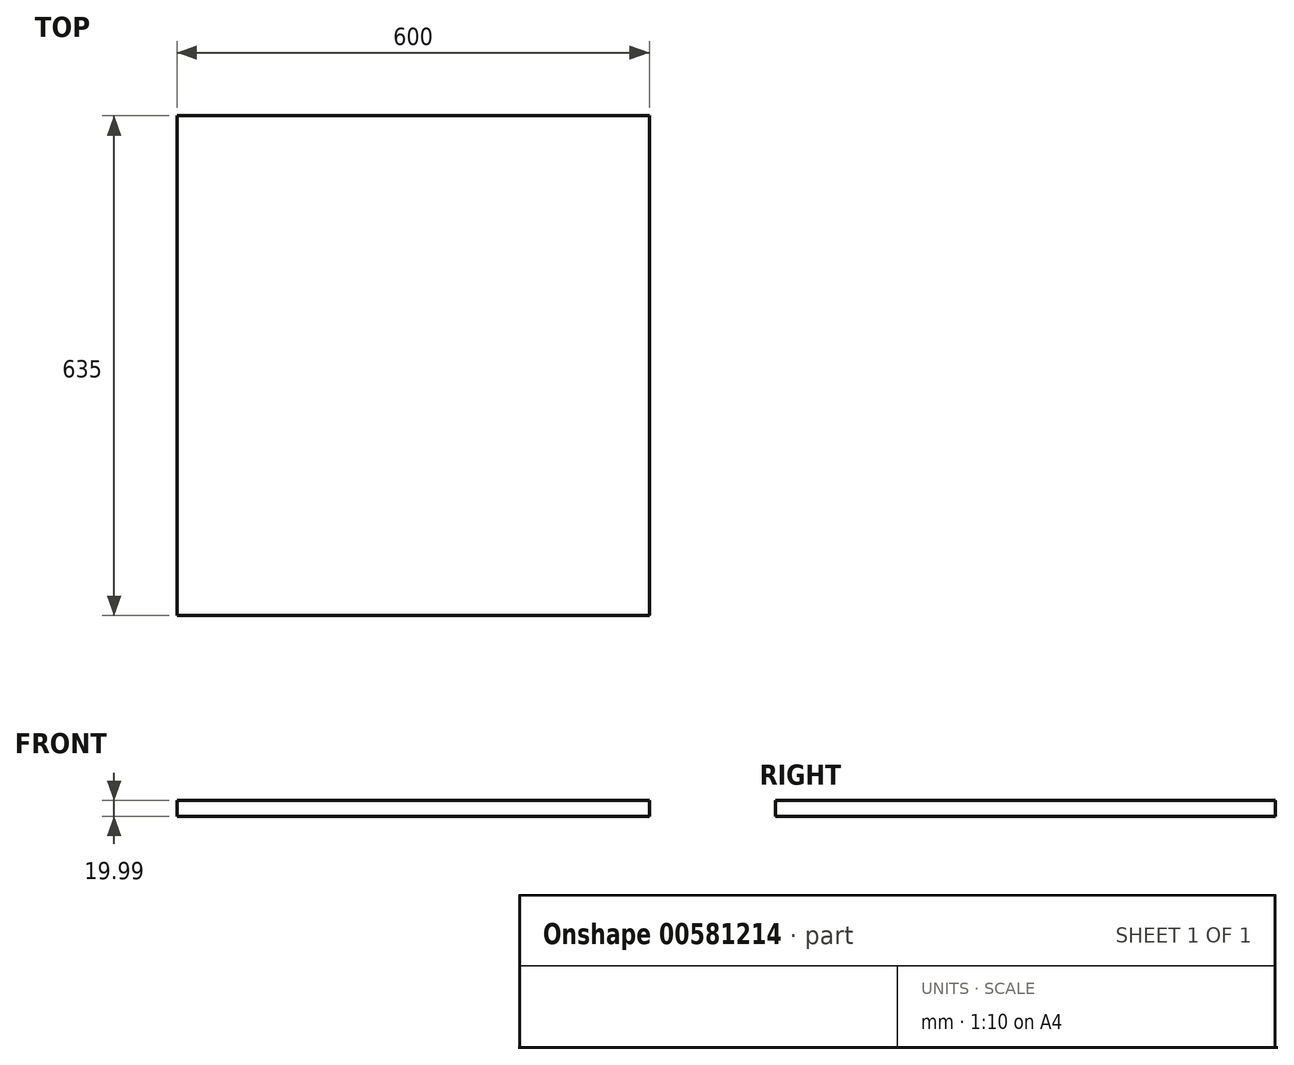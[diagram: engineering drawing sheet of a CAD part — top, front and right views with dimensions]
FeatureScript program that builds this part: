
annotation { "Feature Type Name" : "Feature", "Feature Type Description" : "" }
export const myFeature = defineFeature(function(context is Context, id is Id, definition is map)
    precondition{}
    {
        {
            var Q0;
            Q0=qCreatedBy(makeId("Top.planeOp"),FACE);
            var sketch = newSketch(context, id + "F0", { "sketchPlane" : qUnion([Q0])});
            skLineSegment(sketch, "E0.bottom", {"start": v(300, 317.5) * mm, "end": v(-300, 317.5) * mm});
            skLineSegment(sketch, "E0.top", {"start": v(300, -317.5) * mm, "end": v(-300, -317.5) * mm});
            skLineSegment(sketch, "E0.left", {"start": v(300, 317.5) * mm, "end": v(300, -317.5) * mm});
            skLineSegment(sketch, "E0.right", {"start": v(-300, 317.5) * mm, "end": v(-300, -317.5) * mm});
            skPoint(sketch, "E0.middle", {"position": v(0, 0) * mm});
            skSolve(sketch);
        }
        {
            var Q0;
            Q0 = qSketchRegion(id + "F0", true);
            extrude(context, id + "F1", {"entities" : qUnion([Q0]), "depth" : 19.99 * mm, "offsetDistance" : 25.4 * mm});
        }
    });
